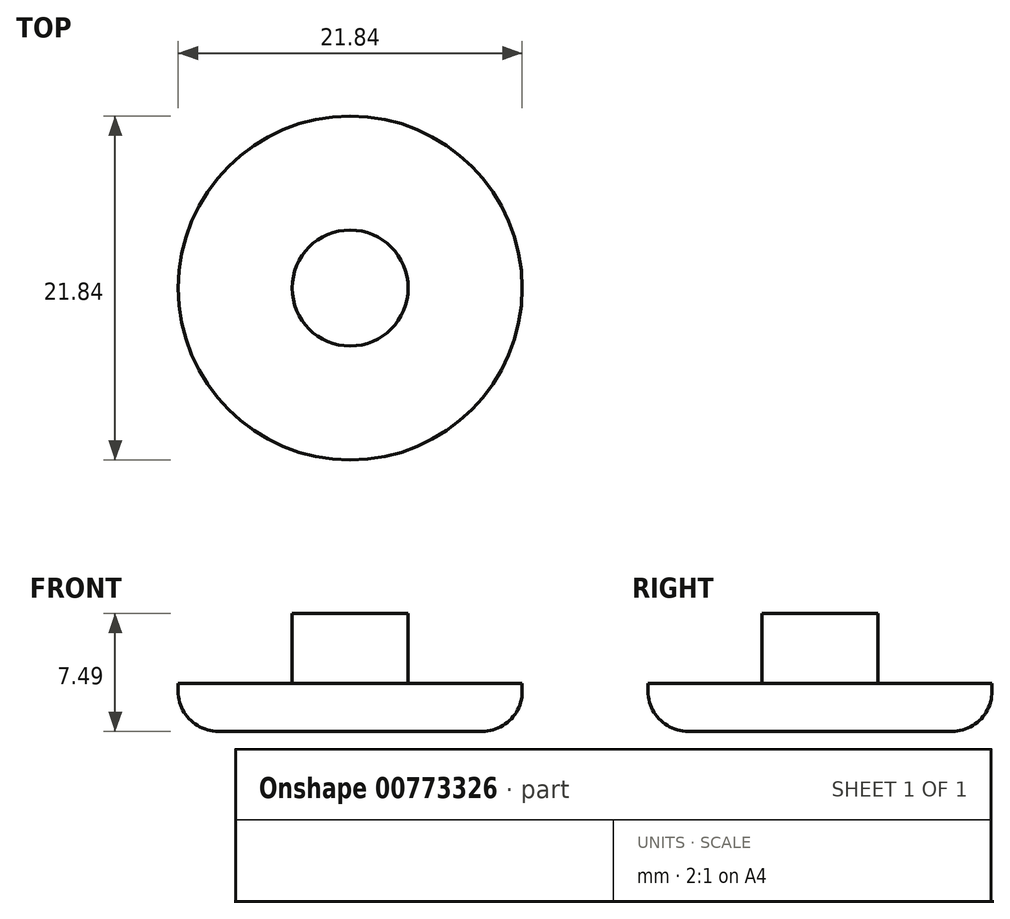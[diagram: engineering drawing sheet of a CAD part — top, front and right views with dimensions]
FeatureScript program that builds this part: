
annotation { "Feature Type Name" : "Feature", "Feature Type Description" : "" }
export const myFeature = defineFeature(function(context is Context, id is Id, definition is map)
    precondition{}
    {
        {
            var Q0;
            Q0=qCreatedBy(makeId("Top.planeOp"),FACE);
            var sketch = newSketch(context, id + "F0", { "sketchPlane" : qUnion([Q0])});
            skCircle(sketch, "E0", {"center": v(0, 0) * mm, "radius": 10.92 * mm});
            skSolve(sketch);
        }
        {
            var Q0;
            Q0 = qSketchRegion(id + "F0", true);
            extrude(context, id + "F1", {"entities" : qUnion([Q0]), "depth" : 3.05 * mm, "offsetDistance" : 25.4 * mm});
        }
        {
            var Q0;
            Q0=makeQuery(id+"F1.opExtrude","CAP_EDGE",EDGE,{"disambiguationData":[OSD([sQuery(id+"F0.wireOp",EDGE,"E0")])],"isStart":true});
            fillet(context, id + "F2", {"entities" : qUnion([Q0]), "radius" : 2.54 * mm, "tangentPropagation" : true, "allowEdgeOverflow" : false});
        }
        {
            var Q0;
            Q0=makeQuery(id+"F1.opExtrude","CAP_FACE",FACE,{"disambiguationData":[OSD([sQuery(id+"F0.wireOp",EDGE,"E0")])],"isStart":false});
            var sketch = newSketch(context, id + "F3", { "sketchPlane" : qUnion([Q0])});
            skCircle(sketch, "E1", {"center": v(0, 0) * mm, "radius": 3.68 * mm});
            skSolve(sketch);
        }
        {
            var Q0;
            Q0 = qSketchRegion(id + "F3", true);
            extrude(context, id + "F4", {"entities" : qUnion([Q0]), "operationType" : NewBodyOperationType.ADD, "depth" : 4.44 * mm, "offsetDistance" : 25.4 * mm});
        }
    });
